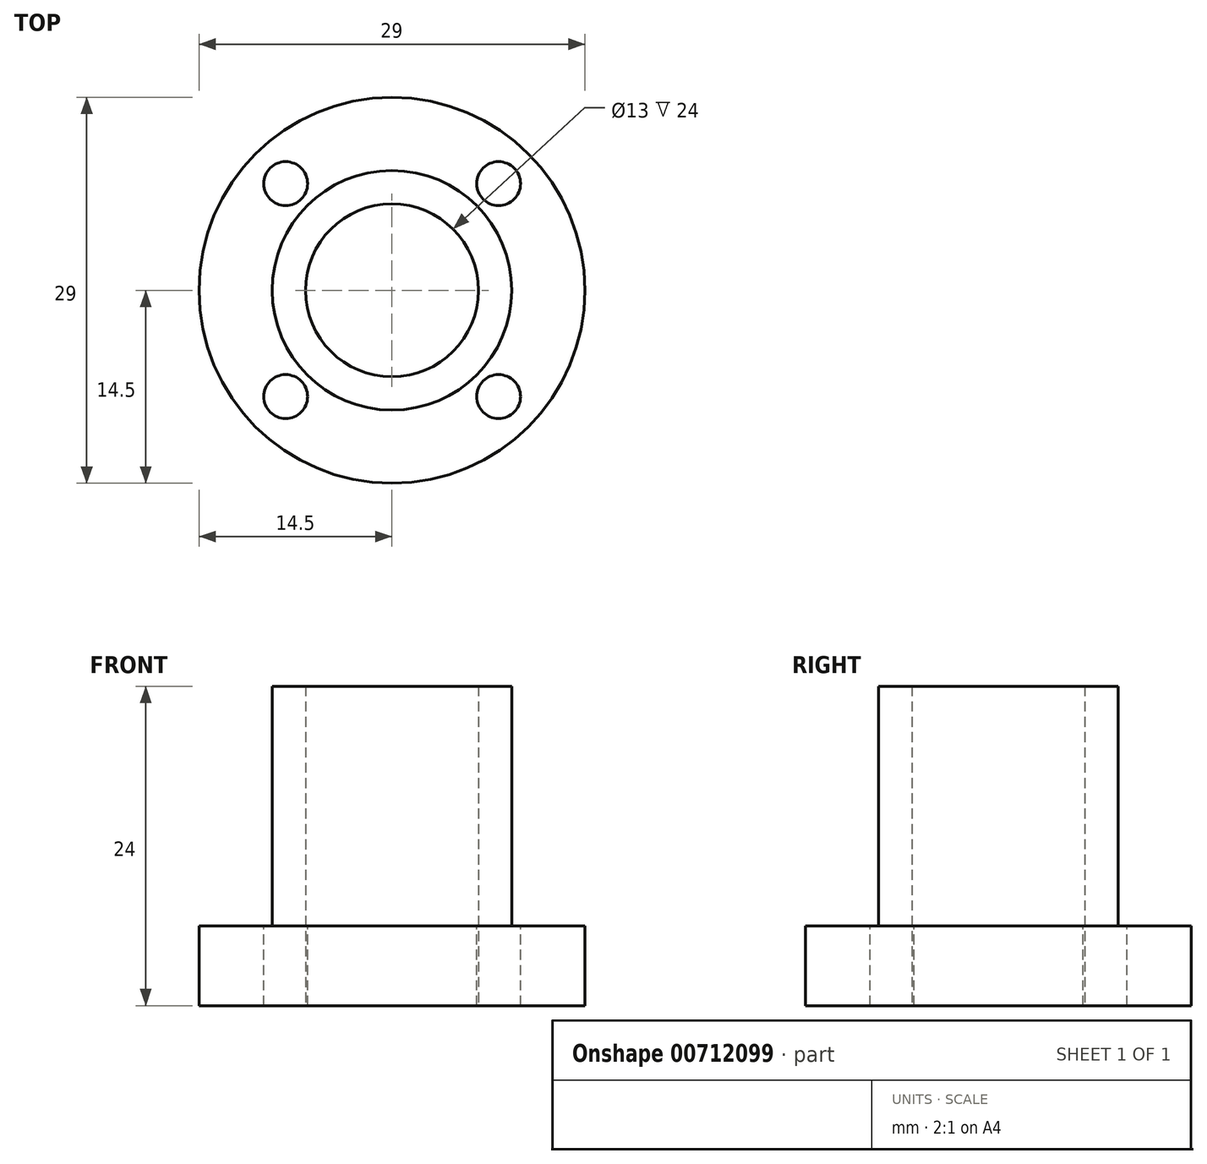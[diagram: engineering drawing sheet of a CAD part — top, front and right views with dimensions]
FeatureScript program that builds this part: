
annotation { "Feature Type Name" : "Feature", "Feature Type Description" : "" }
export const myFeature = defineFeature(function(context is Context, id is Id, definition is map)
    precondition{}
    {
        {
            var Q0;
            Q0=qCreatedBy(makeId("Top.planeOp"),FACE);
            var sketch = newSketch(context, id + "F0", { "sketchPlane" : qUnion([Q0])});
            skCircle(sketch, "E0", {"center": v(0, 0) * mm, "radius": 14.5 * mm});
            skCircle(sketch, "E1", {"center": v(0, 0) * mm, "radius": 9 * mm});
            skSolve(sketch);
        }
        {
            var Q0;
            Q0 = qSketchRegion(id + "F0", true);
            var Q1;
            Q1=makeQuery(id+"F0.imprint","IMPRINT",FACE,{"disambiguationData":[TD([[makeQuery(id+"F0.imprint","IMPRINT",EDGE,{"derivedFrom":sQuery(id+"F0.wireOp",EDGE,"E1")}),1.0]])]});
            extrude(context, id + "F1", {"entities" : qUnion([Q0, Q1]), "oppositeDirection" : true, "depth" : 6 * mm, "offsetDistance" : 25 * mm});
        }
        {
            var Q0;
            Q0=makeQuery(id+"F0.imprint","IMPRINT",FACE,{"disambiguationData":[TD([[makeQuery(id+"F0.imprint","IMPRINT",EDGE,{"derivedFrom":sQuery(id+"F0.wireOp",EDGE,"E1")}),1.0]])]});
            extrude(context, id + "F2", {"entities" : qUnion([Q0]), "operationType" : NewBodyOperationType.ADD, "depth" : 18 * mm, "offsetDistance" : 25 * mm});
        }
        {
            var Q0;
            Q0=makeQuery(id+"F2.opExtrude","CAP_FACE",FACE,{"disambiguationData":[OSD([sQuery(id+"F0.wireOp",EDGE,"E1")])],"isStart":false});
            var sketch = newSketch(context, id + "F3", { "sketchPlane" : qUnion([Q0])});
            skPoint(sketch, "E2", {"position": v(0, 0) * mm});
            skSolve(sketch);
        }
        {
            var Q0;
            Q0=sQuery(id+"F3.wireOp",VERTEX,"E2");
            var Q1;
            Q1=makeQuery(id+"F1.opExtrude","SWEPT_BODY",BODY,{"disambiguationData":[OSD([sQuery(id+"F0.wireOp",EDGE,"E0")])]});
            hole(context, id + "F4", {"style" : HoleStyle.SIMPLE, "endStyle" : HoleEndStyle.THROUGH, "holeDiameter" : 13 * mm, "majorDiameter" : 5 * mm, "tappedDepth" : 12 * mm, "tapClearance" : 3, "locations" : qUnion([Q0]), "scope" : qUnion([Q1]), "startStyle" : HoleStartStyle.PART});
        }
        {
            var Q0;
            Q0=makeQuery(id+"F1.opExtrude","CAP_FACE",FACE,{"disambiguationData":[OSD([sQuery(id+"F0.wireOp",EDGE,"E0")])],"isStart":false});
            var sketch = newSketch(context, id + "F5", { "sketchPlane" : qUnion([Q0])});
            skLineSegment(sketch, "E3", {"start": v(0.01, 25.8) * mm, "end": v(0.01, -24.41) * mm, "construction": true});
            skLineSegment(sketch, "E4", {"start": v(20.48, -0.02) * mm, "end": v(-22.25, -0.02) * mm, "construction": true});
            skLineSegment(sketch, "E5.0", {"start": v(20.48, 7.98) * mm, "end": v(-22.25, 7.98) * mm, "construction": true});
            skLineSegment(sketch, "E6.0", {"start": v(20.48, -8.02) * mm, "end": v(-22.25, -8.02) * mm, "construction": true});
            skLineSegment(sketch, "E7.0", {"start": v(8.01, 25.8) * mm, "end": v(8.01, -24.41) * mm, "construction": true});
            skLineSegment(sketch, "E8.0", {"start": v(-7.99, 25.8) * mm, "end": v(-7.99, -24.41) * mm, "construction": true});
            skPoint(sketch, "E9", {"position": v(8.01, 7.98) * mm});
            skPoint(sketch, "E10", {"position": v(8.01, -8.02) * mm});
            skPoint(sketch, "E11", {"position": v(-7.99, -8.02) * mm});
            skPoint(sketch, "E12", {"position": v(-7.99, 7.98) * mm});
            skPoint(sketch, "E13", {"position": v(0.01, -0.02) * mm});
            skSolve(sketch);
        }
        {
            var Q0;
            Q0=sQuery(id+"F5.wireOp",VERTEX,"E9");
            var Q1;
            Q1=sQuery(id+"F5.wireOp",VERTEX,"E10");
            var Q2;
            Q2=sQuery(id+"F5.wireOp",VERTEX,"E11");
            var Q3;
            Q3=sQuery(id+"F5.wireOp",VERTEX,"E12");
            var Q4;
            Q4=makeQuery(id+"F1.opExtrude","SWEPT_BODY",BODY,{"disambiguationData":[OSD([sQuery(id+"F0.wireOp",EDGE,"E0")])]});
            hole(context, id + "F6", {"style" : HoleStyle.SIMPLE, "endStyle" : HoleEndStyle.THROUGH, "standardTappedOrClearance" : lookupTablePath({ "standard" : "ISO", "fit" : "Normal", "size" : "M3", "type" : "Clearance" }), "standardBlindInLast" : lookupTablePath({ "fit" : "Standard", "standard" : "ISO", "size" : "M3", "type" : "Clearance" }), "holeDiameter" : 3.3 * mm, "majorDiameter" : 5 * mm, "tappedDepth" : 12 * mm, "tapClearance" : 3, "locations" : qUnion([Q0, Q1, Q2, Q3]), "scope" : qUnion([Q4]), "startStyle" : HoleStartStyle.PART});
        }
    });
